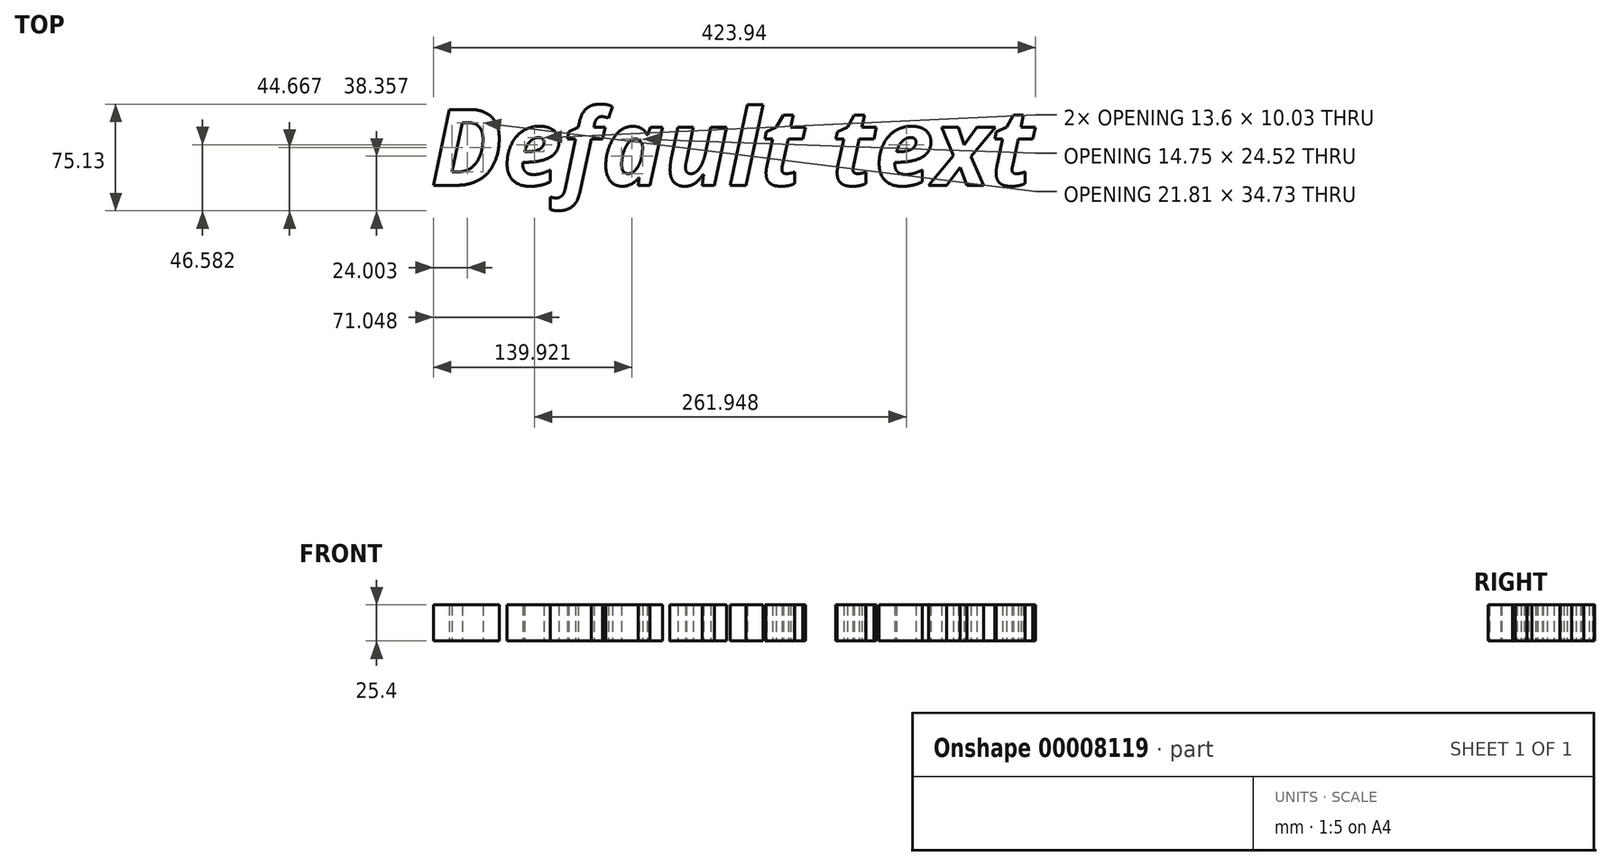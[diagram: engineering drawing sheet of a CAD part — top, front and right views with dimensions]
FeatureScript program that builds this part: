
annotation { "Feature Type Name" : "Feature", "Feature Type Description" : "" }
export const myFeature = defineFeature(function(context is Context, id is Id, definition is map)
    precondition{}
    {
        {
            var Q0;
            Q0=qCreatedBy(makeId("Top.planeOp"),FACE);
            var sketch = newSketch(context, id + "F0", { "sketchPlane" : qUnion([Q0])});
            skText(sketch, "E0", { "text": "Default text", "fontName": "OpenSans-BoldItalic.ttf"});
            const initialGuessF0  = {"E0": [-0.1081, -0.0538, 1, 0, 0.0538]};
            skSetInitialGuess(sketch, initialGuessF0);
            skSolve(sketch);
        }
        {
            var Q0;
            Q0 = qSketchRegion(id + "F0", true);
            extrude(context, id + "F1", {"entities" : qUnion([Q0]), "depth" : 25.4 * mm});
        }
    });
